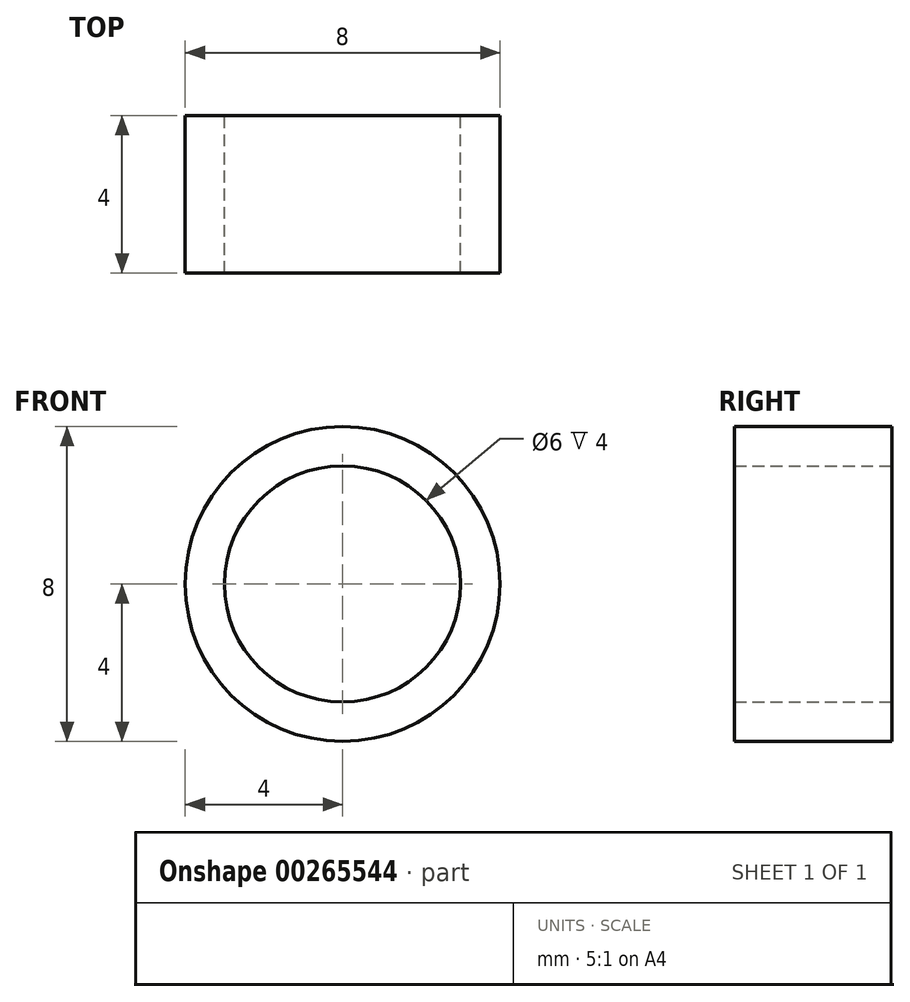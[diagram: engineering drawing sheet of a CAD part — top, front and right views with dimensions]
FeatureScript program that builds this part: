
annotation { "Feature Type Name" : "Feature", "Feature Type Description" : "" }
export const myFeature = defineFeature(function(context is Context, id is Id, definition is map)
    precondition{}
    {
        {
            var Q0;
            Q0=qCreatedBy(makeId("Front.planeOp"),FACE);
            var sketch = newSketch(context, id + "F0", { "sketchPlane" : qUnion([Q0])});
            skCircle(sketch, "E0", {"center": v(0, 0) * mm, "radius": 4 * mm});
            skCircle(sketch, "E1", {"center": v(0, 0) * mm, "radius": 3 * mm});
            skSolve(sketch);
        }
        {
            var Q0;
            Q0=makeQuery(id+"F0.imprint","IMPRINT",FACE,{"disambiguationData":[TD([[makeQuery(id+"F0.imprint","IMPRINT",EDGE,{"derivedFrom":sQuery(id+"F0.wireOp",EDGE,"E0")}),1.0]])]});
            extrude(context, id + "F1", {"entities" : qUnion([Q0]), "depth" : 4 * mm});
        }
    });
